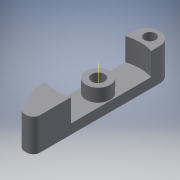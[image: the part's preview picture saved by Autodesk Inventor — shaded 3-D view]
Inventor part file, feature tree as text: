
AUTODESK INVENTOR PART (.ipt)
format: ipt  version: 2016 (Build 200138000, 138)  size: 210,432 bytes
history: native  units: mm
features: extrude x8, sketch x8, projected_geometry x6, fillet x3, other x1
ambient origin geometry x8: Origin, YZ Plane, XZ Plane, XY Plane, X Axis, Y Axis, Z Axis, Center Point
bodies: Solid1 (feature_tree)
feature tree (26):
  extrude  "Extrusion1"  Depth=10.0mm TaperAngle=0.0deg
  extrude  "Extrusion2"  Depth=26.0mm
  extrude  "Extrusion3"  Depth=4.0mm
  extrude  "Extrusion4"  Depth=7.0mm
  extrude  "Extrusion8"  Depth=3.0mm
  extrude  "Extrusion10"  Depth=2.0mm
  other  "Work Axis1"
  extrude  "Extrusion11"  Depth=3.0mm TaperAngle=0.0deg
  extrude  "Extrusion9"  Depth=4.0mm TaperAngle=0.0deg
  fillet  "Fillet4"  Radius=2.0mm
  fillet  "Fillet1"  Radius=3.0mm
  fillet  "Fillet2"  Radius=1.0mm
  sketch  "Sketch1"  dims[d0=4.0mm d1=10.0mm d2=0.0mm]
  sketch  "Sketch2"  dims[d3=26.0mm d4=7.5mm]
  projected_geometry  "Projected Loop1"
  sketch  "Sketch3"  dims[d5=7.0mm d6=0.0mm d7=4.0mm]
  projected_geometry  "Projected Loop2"
  sketch  "Sketch4"  dims[d8=7.0mm d9=0.0mm d10=6.4mm]
  projected_geometry  "Projected Loop3"
  sketch  "Sketch8"  dims[d11=3.0mm d12=0.0mm d17=30.0mm]
  projected_geometry  "Projected Loop7"
  sketch  "Sketch9"  dims[d25=2.0mm d26=1.0mm]
  sketch  "Sketch10"  dims[d28=3.5mm d29=3.0mm d30=0.0mm]
  projected_geometry  "Projected Loop8"
  sketch  "Sketch12"  dims[d31=4.0mm d32=4.0mm d33=0.0mm d34=2.0mm d35=3.0mm d36=0.0mm d40=1.0mm d41=5.402024mm d42=5.0mm d43=10.0mm d44=0.0mm d45=1.151345mm d46=2.0mm]
  projected_geometry  "Projected Loop10"
